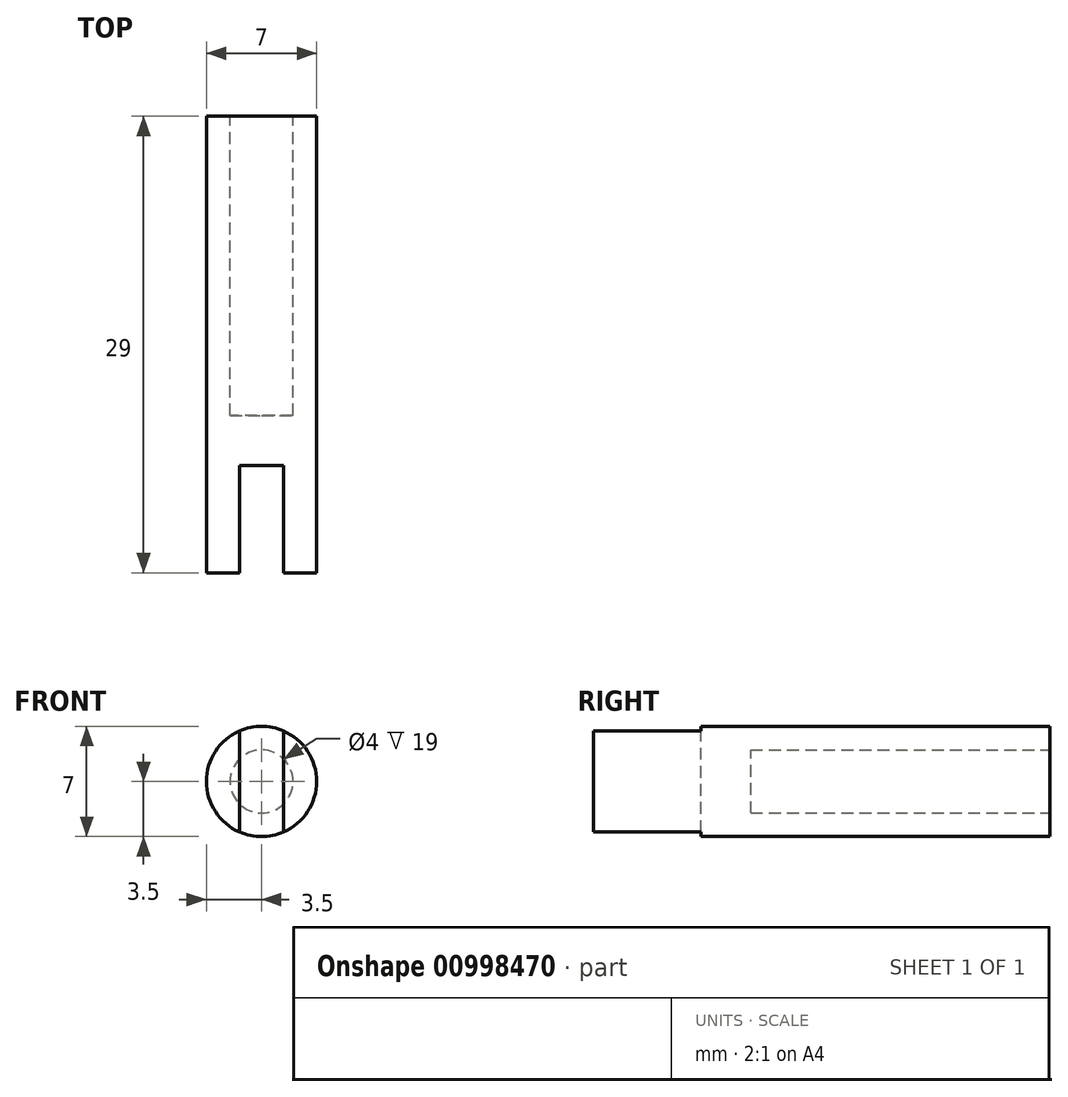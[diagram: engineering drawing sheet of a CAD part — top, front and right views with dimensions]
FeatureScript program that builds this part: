
annotation { "Feature Type Name" : "Feature", "Feature Type Description" : "" }
export const myFeature = defineFeature(function(context is Context, id is Id, definition is map)
    precondition{}
    {
        {
            var Q0;
            Q0=qCreatedBy(makeId("Front.planeOp"),FACE);
            var sketch = newSketch(context, id + "F0", { "sketchPlane" : qUnion([Q0])});
            skCircle(sketch, "E0", {"center": v(0, 0) * mm, "radius": 2 * mm});
            skSolve(sketch);
        }
        {
            var Q0;
            Q0=qCreatedBy(makeId("Front.planeOp"),FACE);
            var sketch = newSketch(context, id + "F1", { "sketchPlane" : qUnion([Q0])});
            skCircle(sketch, "E1", {"center": v(0, 0) * mm, "radius": 3.5 * mm});
            skSolve(sketch);
        }
        {
            var Q0;
            Q0 = qSketchRegion(id + "F1", true);
            extrude(context, id + "F2", {"entities" : qUnion([Q0]), "depth" : 29 * mm, "offsetDistance" : 25 * mm});
        }
        {
            var Q0;
            Q0 = qSketchRegion(id + "F0", true);
            extrude(context, id + "F3", {"entities" : qUnion([Q0]), "operationType" : NewBodyOperationType.REMOVE, "depth" : 19 * mm, "offsetDistance" : 25 * mm});
        }
        {
            var Q0;
            Q0=qCreatedBy(makeId("Top.planeOp"),FACE);
            var sketch = newSketch(context, id + "F4", { "sketchPlane" : qUnion([Q0])});
            skLineSegment(sketch, "E2.bottom", {"start": v(1.4, -30.07) * mm, "end": v(-1.4, -30.07) * mm});
            skLineSegment(sketch, "E2.top", {"start": v(1.4, -22.17) * mm, "end": v(-1.4, -22.17) * mm});
            skLineSegment(sketch, "E2.left", {"start": v(1.4, -30.07) * mm, "end": v(1.4, -22.17) * mm});
            skLineSegment(sketch, "E2.right", {"start": v(-1.4, -30.07) * mm, "end": v(-1.4, -22.17) * mm});
            skPoint(sketch, "E2.middle", {"position": v(0, -26.12) * mm});
            skSolve(sketch);
        }
        {
            var Q0;
            Q0=makeQuery(id+"F4.imprint","IMPRINT",FACE,{"disambiguationData":[TD([[makeQuery(id+"F4.imprint","IMPRINT",EDGE,{"derivedFrom":sQuery(id+"F4.wireOp",EDGE,"E2.bottom")}),-1.0]])]});
            extrude(context, id + "F5", {"entities" : qUnion([Q0]), "operationType" : NewBodyOperationType.REMOVE, "endBound" : BoundingType.SYMMETRIC, "oppositeDirection" : true, "depth" : 25 * mm, "offsetDistance" : 25 * mm});
        }
    });
